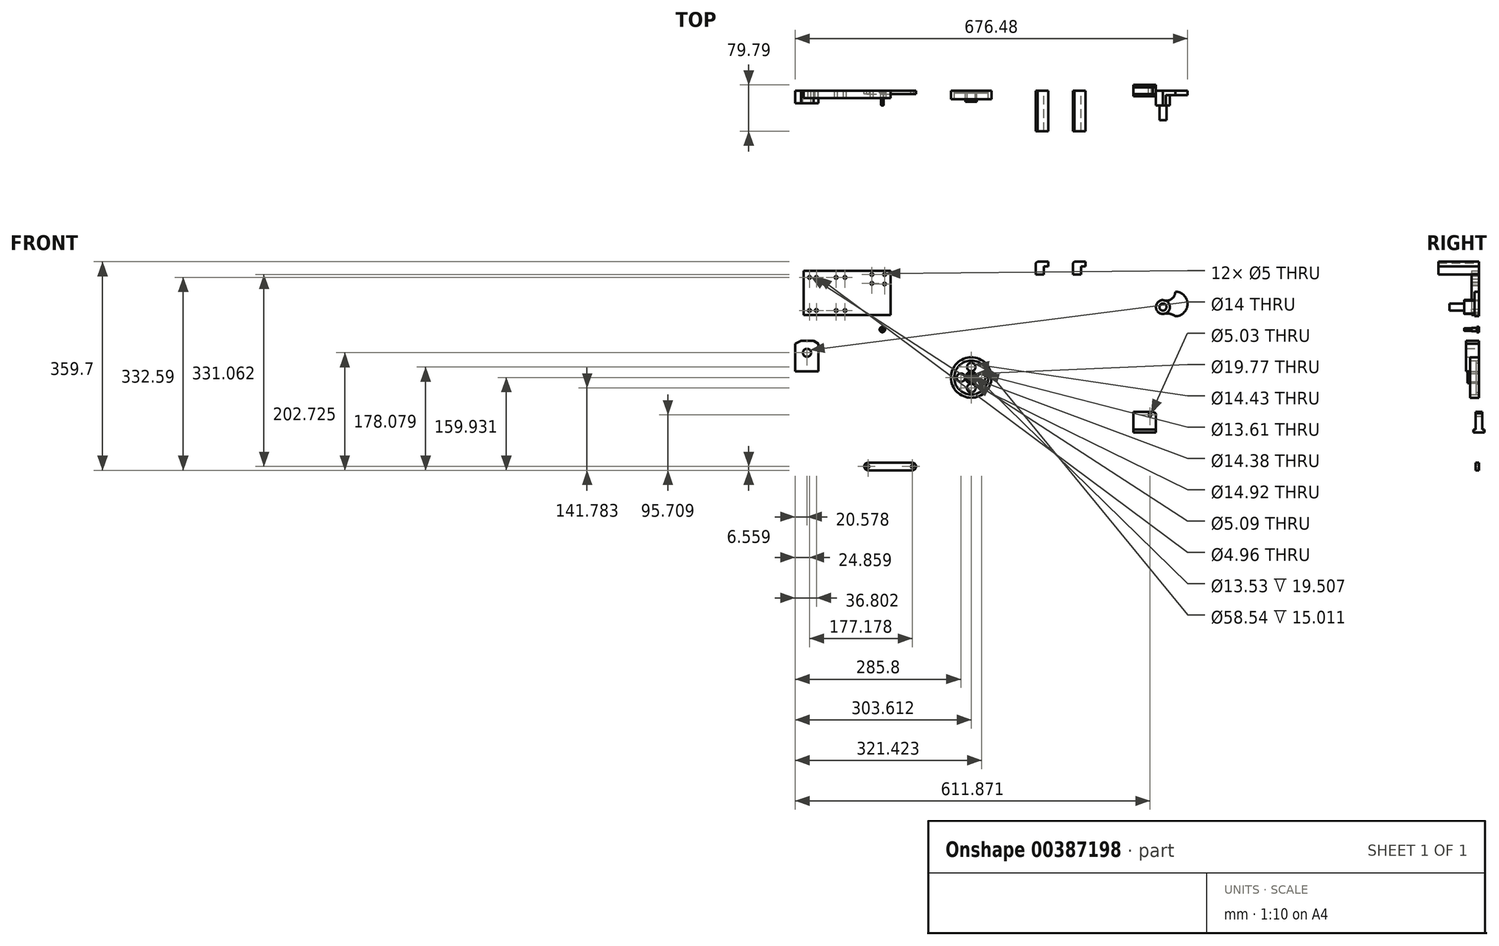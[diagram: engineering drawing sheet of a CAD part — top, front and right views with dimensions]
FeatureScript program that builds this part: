
annotation { "Feature Type Name" : "Feature", "Feature Type Description" : "" }
export const myFeature = defineFeature(function(context is Context, id is Id, definition is map)
    precondition{}
    {
        {
            var Q0;
            Q0=qCreatedBy(makeId("Front.planeOp"),FACE);
            var sketch = newSketch(context, id + "F0", { "sketchPlane" : qUnion([Q0])});
            skLineSegment(sketch, "E0.bottom", {"start": v(-272.23, -114.03) * mm, "end": v(-232.23, -114.03) * mm});
            skLineSegment(sketch, "E0.top", {"start": v(-272.23, -162.01) * mm, "end": v(-232.23, -162.01) * mm});
            skLineSegment(sketch, "E0.left", {"start": v(-272.23, -114.03) * mm, "end": v(-272.23, -162.01) * mm});
            skLineSegment(sketch, "E0.right", {"start": v(-232.23, -114.03) * mm, "end": v(-232.23, -162.01) * mm});
            skLineSegment(sketch, "E1", {"start": v(-232.23, -114.03) * mm, "end": v(-240.58, -109.22) * mm});
            skLineSegment(sketch, "E2", {"start": v(-240.58, -109.22) * mm, "end": v(-262.01, -109.22) * mm});
            skLineSegment(sketch, "E3", {"start": v(-262.01, -109.22) * mm, "end": v(-272.23, -114.03) * mm});
            skCircle(sketch, "E4", {"center": v(-251.65, -129.87) * mm, "radius": 7 * mm});
            skLineSegment(sketch, "E5.bottom", {"start": v(-146.57, -319.47) * mm, "end": v(-70.2, -319.47) * mm});
            skLineSegment(sketch, "E5.top", {"start": v(-146.57, -332.59) * mm, "end": v(-70.2, -332.59) * mm});
            skArc(sketch, "E6", {"start": v(-70.2, -332.59) * mm, "mid": v(-63.64, -326.03) * mm, "end": v(-70.2, -319.47) * mm});
            skArc(sketch, "E7", {"start": v(-146.57, -319.47) * mm, "mid": v(-153.13, -326.03) * mm, "end": v(-146.57, -332.59) * mm});
            skCircle(sketch, "E8", {"center": v(-146.57, -326.03) * mm, "radius": 2.5 * mm});
            skCircle(sketch, "E9", {"center": v(-70.2, -326.03) * mm, "radius": 2.5 * mm});
            skLineSegment(sketch, "E10.bottom", {"start": v(310.57, -262.58) * mm, "end": v(349.62, -262.58) * mm});
            skLineSegment(sketch, "E10.top", {"start": v(310.57, -267.24) * mm, "end": v(349.62, -267.24) * mm});
            skLineSegment(sketch, "E10.left", {"start": v(310.57, -262.58) * mm, "end": v(310.57, -267.24) * mm});
            skLineSegment(sketch, "E10.right", {"start": v(349.62, -262.58) * mm, "end": v(349.62, -267.24) * mm});
            skLineSegment(sketch, "E11.top", {"start": v(310.57, -232.03) * mm, "end": v(344.59, -232.03) * mm});
            skLineSegment(sketch, "E11.left", {"start": v(310.57, -262.58) * mm, "end": v(310.57, -232.03) * mm});
            skLineSegment(sketch, "E11.right", {"start": v(349.62, -262.58) * mm, "end": v(349.62, -234.65) * mm});
            skLineSegment(sketch, "E12", {"start": v(344.59, -232.03) * mm, "end": v(349.62, -234.65) * mm});
            skPoint(sketch, "E13.orphan", {"position": v(349.62, -232.03) * mm});
            skCircle(sketch, "E14", {"center": v(339.64, -236.88) * mm, "radius": 2.52 * mm});
            skLineSegment(sketch, "E15.bottom", {"start": v(-257.4, 11.32) * mm, "end": v(-107.39, 11.32) * mm});
            skLineSegment(sketch, "E15.top", {"start": v(-257.4, -64.67) * mm, "end": v(-107.39, -64.67) * mm});
            skLineSegment(sketch, "E15.left", {"start": v(-257.4, 11.32) * mm, "end": v(-257.4, -64.67) * mm});
            skLineSegment(sketch, "E15.right", {"start": v(-107.39, 11.32) * mm, "end": v(-107.39, -64.67) * mm});
            skCircle(sketch, "E16", {"center": v(-247.37, 0) * mm, "radius": 2.55 * mm});
            skCircle(sketch, "E17", {"center": v(-235.43, 0) * mm, "radius": 2.48 * mm});
            skCircle(sketch, "E18", {"center": v(-235.43, -56.99) * mm, "radius": 2.5 * mm});
            skCircle(sketch, "E19", {"center": v(-247.37, -56.99) * mm, "radius": 2.5 * mm});
            skCircle(sketch, "E20", {"center": v(-201.5, -56.99) * mm, "radius": 2.5 * mm});
            skCircle(sketch, "E21", {"center": v(-186.19, -56.99) * mm, "radius": 2.5 * mm});
            skCircle(sketch, "E22", {"center": v(-201.5, 0) * mm, "radius": 2.5 * mm});
            skCircle(sketch, "E23", {"center": v(-186.19, 0) * mm, "radius": 2.5 * mm});
            skCircle(sketch, "E24", {"center": v(-139.86, 5.03) * mm, "radius": 2.5 * mm});
            skCircle(sketch, "E25", {"center": v(-139.86, -10.28) * mm, "radius": 2.5 * mm});
            skCircle(sketch, "E26", {"center": v(-118.04, 5.03) * mm, "radius": 2.5 * mm});
            skCircle(sketch, "E27", {"center": v(-118.04, -11.43) * mm, "radius": 2.5 * mm});
            skLineSegment(sketch, "E28.bottom", {"start": v(142.44, 5.11) * mm, "end": v(156.44, 5.11) * mm});
            skLineSegment(sketch, "E28.top", {"start": v(142.44, 19.1) * mm, "end": v(156.44, 19.1) * mm});
            skLineSegment(sketch, "E28.left", {"start": v(142.44, 5.11) * mm, "end": v(142.44, 19.1) * mm});
            skLineSegment(sketch, "E28.right", {"start": v(156.44, 5.11) * mm, "end": v(156.44, 19.1) * mm});
            skLineSegment(sketch, "E29.bottom", {"start": v(142.44, 19.1) * mm, "end": v(164.44, 19.1) * mm});
            skLineSegment(sketch, "E29.top", {"start": v(145.53, 27.11) * mm, "end": v(164.44, 27.11) * mm});
            skLineSegment(sketch, "E29.left", {"start": v(142.44, 19.1) * mm, "end": v(142.44, 24.73) * mm});
            skLineSegment(sketch, "E29.right", {"start": v(164.44, 19.1) * mm, "end": v(164.44, 27.11) * mm});
            skLineSegment(sketch, "E30", {"start": v(145.53, 27.11) * mm, "end": v(142.44, 24.73) * mm});
            skPoint(sketch, "E31.oppositeSnap0", {"position": v(153.44, 19.1) * mm});
            skLineSegment(sketch, "E31.bottom", {"start": v(206.6, 5.11) * mm, "end": v(220.6, 5.11) * mm});
            skLineSegment(sketch, "E31.top", {"start": v(206.6, 19.1) * mm, "end": v(220.6, 19.1) * mm});
            skLineSegment(sketch, "E31.left", {"start": v(206.6, 5.11) * mm, "end": v(206.6, 19.1) * mm});
            skLineSegment(sketch, "E31.right", {"start": v(220.6, 5.11) * mm, "end": v(220.6, 19.1) * mm});
            skLineSegment(sketch, "E32.bottom", {"start": v(206.6, 19.1) * mm, "end": v(228.6, 19.1) * mm});
            skLineSegment(sketch, "E32.top", {"start": v(209.4, 27.11) * mm, "end": v(228.6, 27.11) * mm});
            skLineSegment(sketch, "E32.right", {"start": v(228.6, 19.1) * mm, "end": v(228.6, 27.11) * mm});
            skLineSegment(sketch, "E33", {"start": v(209.4, 27.11) * mm, "end": v(206.6, 24.7) * mm});
            skLineSegment(sketch, "E34", {"start": v(206.6, 24.7) * mm, "end": v(206.6, 19.1) * mm});
            skCircle(sketch, "E35", {"center": v(-121.83, -89.85) * mm, "radius": 2 * mm});
            skCircle(sketch, "E36", {"center": v(-121.83, -89.85) * mm, "radius": 2.87 * mm});
            skCircle(sketch, "E37", {"center": v(-121.83, -89.85) * mm, "radius": 4.6 * mm});
            skArc(sketch, "E38", {"start": v(383.1, -66.86) * mm, "mid": v(404.25, -45.72) * mm, "end": v(383.1, -24.58) * mm});
            skLineSegment(sketch, "E39", {"start": v(383.1, -24.58) * mm, "end": v(383.1, -66.86) * mm});
            skArc(sketch, "E40", {"start": v(361.79, -39) * mm, "mid": v(376.27, -37.44) * mm, "end": v(383.1, -24.58) * mm});
            skCircle(sketch, "E41", {"center": v(361.79, -51.03) * mm, "radius": 12.04 * mm});
            skArc(sketch, "E42", {"start": v(383.1, -66.86) * mm, "mid": v(372.87, -62.57) * mm, "end": v(361.79, -63.07) * mm});
            skCircle(sketch, "E43", {"center": v(361.79, -51.03) * mm, "radius": 6.14 * mm});
            skCircle(sketch, "E44", {"center": v(31.38, -172.66) * mm, "radius": 34.87 * mm});
            skCircle(sketch, "E45", {"center": v(31.38, -172.66) * mm, "radius": 29.27 * mm});
            skCircle(sketch, "E46", {"center": v(31.38, -172.66) * mm, "radius": 9.88 * mm});
            skCircle(sketch, "E47", {"center": v(31.38, -172.66) * mm, "radius": 6.76 * mm});
            skCircle(sketch, "E48", {"center": v(31.38, -154.51) * mm, "radius": 7.22 * mm});
            skCircle(sketch, "E49", {"center": v(49.2, -172.66) * mm, "radius": 6.8 * mm});
            skCircle(sketch, "E50", {"center": v(13.57, -172.66) * mm, "radius": 7.2 * mm});
            skCircle(sketch, "E51", {"center": v(31.38, -190.8) * mm, "radius": 7.46 * mm});
            skSolve(sketch);
        }
        {
            var Q0;
            Q0=makeQuery(id+"F0.imprint","IMPRINT",FACE,{"disambiguationData":[TD([[makeQuery(id+"F0.imprint","IMPRINT",EDGE,{"derivedFrom":sQuery(id+"F0.wireOp",EDGE,"E35")}),1.0]])]});
            extrude(context, id + "F1", {"entities" : qUnion([Q0]), "depth" : 25.4 * mm});
        }
        {
            var Q0;
            Q0=makeQuery(id+"F0.imprint","IMPRINT",FACE,{"disambiguationData":[TD([[makeQuery(id+"F0.imprint","IMPRINT",EDGE,{"derivedFrom":sQuery(id+"F0.wireOp",EDGE,"E35")}),-1.0]])]});
            extrude(context, id + "F2", {"entities" : qUnion([Q0]), "operationType" : NewBodyOperationType.ADD, "depth" : 12.7 * mm});
        }
        {
            var Q0;
            Q0=makeQuery(id+"F0.imprint","IMPRINT",FACE,{"disambiguationData":[TD([[makeQuery(id+"F0.imprint","IMPRINT",EDGE,{"derivedFrom":sQuery(id+"F0.wireOp",EDGE,"E36")}),-1.0]])]});
            extrude(context, id + "F3", {"entities" : qUnion([Q0]), "operationType" : NewBodyOperationType.ADD, "depth" : 3.8 * mm});
        }
        {
            var Q0;
            Q0=makeQuery(id+"F3.opExtrude","CAP_EDGE",EDGE,{"disambiguationData":[OSD([sQuery(id+"F0.wireOp",EDGE,"E37")])],"isStart":true});
            var Q1;
            Q1=makeQuery(id+"F1.opExtrude","CAP_EDGE",EDGE,{"disambiguationData":[OSD([sQuery(id+"F0.wireOp",EDGE,"E35")])],"isStart":false});
            fillet(context, id + "F4", {"entities" : qUnion([Q0, Q1]), "radius" : 0.5 * mm, "tangentPropagation" : true, "allowEdgeOverflow" : false});
        }
        {
            var Q0;
            Q0=makeQuery(id+"F0.imprint","IMPRINT",FACE,{"disambiguationData":[TD([[makeQuery(id+"F0.imprint","IMPRINT",EDGE,{"derivedFrom":sQuery(id+"F0.wireOp",EDGE,"E43")}),1.0]])]});
            extrude(context, id + "F5", {"entities" : qUnion([Q0]), "depth" : 50.8 * mm});
        }
        {
            var Q0;
            Q0=makeQuery(id+"F0.imprint","IMPRINT",FACE,{"disambiguationData":[TD([[makeQuery(id+"F0.imprint","IMPRINT",EDGE,{"derivedFrom":sQuery(id+"F0.wireOp",EDGE,"E43")}),-1.0]])]});
            extrude(context, id + "F6", {"entities" : qUnion([Q0]), "operationType" : NewBodyOperationType.ADD, "depth" : 25.4 * mm});
        }
        {
            var Q0;
            Q0=makeQuery(id+"F0.imprint","IMPRINT",FACE,{"disambiguationData":[TD([[makeQuery(id+"F0.imprint","IMPRINT",EDGE,{"derivedFrom":sQuery(id+"F0.wireOp",EDGE,"E38")}),1.0]])]});
            var Q1;
            {var subQ0=sQuery(id+"F0.wireOp",EDGE,"E39");Q1=makeQuery(id+"F0.imprint","IMPRINT",FACE,{"disambiguationData":[TD([[makeQuery(id+"F0.imprint","IMPRINT",EDGE,{"derivedFrom":subQ0}),-1.0]])]});}
            extrude(context, id + "F7", {"entities" : qUnion([Q0, Q1]), "operationType" : NewBodyOperationType.ADD, "depth" : 7.62 * mm});
        }
        {
            var Q0;
            Q0=makeQuery(id+"F0.imprint","IMPRINT",FACE,{"disambiguationData":[TD([[makeQuery(id+"F0.imprint","IMPRINT",EDGE,{"derivedFrom":sQuery(id+"F0.wireOp",EDGE,"E46")}),1.0]])]});
            extrude(context, id + "F8", {"entities" : qUnion([Q0]), "depth" : 19.5 * mm});
        }
        {
            var Q0;
            Q0=makeQuery(id+"F0.imprint","IMPRINT",FACE,{"disambiguationData":[TD([[makeQuery(id+"F0.imprint","IMPRINT",EDGE,{"derivedFrom":sQuery(id+"F0.wireOp",EDGE,"E44")}),1.0]])]});
            extrude(context, id + "F9", {"entities" : qUnion([Q0]), "depth" : 15 * mm});
        }
        {
            var Q0;
            Q0=makeQuery(id+"F0.imprint","IMPRINT",FACE,{"disambiguationData":[TD([[makeQuery(id+"F0.imprint","IMPRINT",EDGE,{"derivedFrom":sQuery(id+"F0.wireOp",EDGE,"E45")}),1.0]])]});
            extrude(context, id + "F10", {"entities" : qUnion([Q0]), "depth" : 4.24 * mm});
        }
        {
            var Q0;
            Q0=makeQuery(id+"F0.imprint","IMPRINT",FACE,{"disambiguationData":[TD([[makeQuery(id+"F0.imprint","IMPRINT",EDGE,{"derivedFrom":sQuery(id+"F0.wireOp",EDGE,"E15.bottom")}),-1.0]])]});
            extrude(context, id + "F11", {"entities" : qUnion([Q0]), "depth" : 12.7 * mm});
        }
        {
            var Q0;
            Q0=makeQuery(id+"F0.imprint","IMPRINT",FACE,{"disambiguationData":[TD([[makeQuery(id+"F0.imprint","IMPRINT",EDGE,{"derivedFrom":sQuery(id+"F0.wireOp",EDGE,"E0.bottom")}),-1.0]])]});
            var Q1;
            Q1=makeQuery(id+"F0.imprint","IMPRINT",FACE,{"disambiguationData":[TD([[makeQuery(id+"F0.imprint","IMPRINT",EDGE,{"derivedFrom":sQuery(id+"F0.wireOp",EDGE,"E0.bottom")}),1.0]])]});
            extrude(context, id + "F12", {"entities" : qUnion([Q0, Q1]), "depth" : 22 * mm});
        }
        {
            var Q0;
            Q0=makeQuery(id+"F0.imprint","IMPRINT",FACE,{"disambiguationData":[TD([[makeQuery(id+"F0.imprint","IMPRINT",EDGE,{"derivedFrom":sQuery(id+"F0.wireOp",EDGE,"E10.top")}),1.0]])]});
            extrude(context, id + "F13", {"entities" : qUnion([Q0]), "endBound" : BoundingType.SYMMETRIC, "depth" : 19.58 * mm});
        }
        {
            var Q0;
            Q0=makeQuery(id+"F0.imprint","IMPRINT",FACE,{"disambiguationData":[TD([[makeQuery(id+"F0.imprint","IMPRINT",EDGE,{"derivedFrom":sQuery(id+"F0.wireOp",EDGE,"E11.top")}),-1.0]])]});
            extrude(context, id + "F14", {"entities" : qUnion([Q0]), "operationType" : NewBodyOperationType.ADD, "endBound" : BoundingType.SYMMETRIC, "depth" : 11.58 * mm});
        }
        {
            var Q0;
            Q0=makeQuery(id+"F0.imprint","IMPRINT",FACE,{"disambiguationData":[TD([[makeQuery(id+"F0.imprint","IMPRINT",EDGE,{"derivedFrom":sQuery(id+"F0.wireOp",EDGE,"E5.bottom")}),-1.0]])]});
            extrude(context, id + "F15", {"entities" : qUnion([Q0]), "depth" : 5.66 * mm});
        }
        {
            var Q0;
            Q0=makeQuery(id+"F0.imprint","IMPRINT",FACE,{"disambiguationData":[TD([[makeQuery(id+"F0.imprint","IMPRINT",EDGE,{"derivedFrom":sQuery(id+"F0.wireOp",EDGE,"E31.bottom")}),1.0]])]});
            var Q1;
            Q1=makeQuery(id+"F0.imprint","IMPRINT",FACE,{"disambiguationData":[TD([[makeQuery(id+"F0.imprint","IMPRINT",EDGE,{"derivedFrom":sQuery(id+"F0.wireOp",EDGE,"E32.top")}),-1.0]])]});
            var Q2;
            Q2=makeQuery(id+"F0.imprint","IMPRINT",FACE,{"disambiguationData":[TD([[makeQuery(id+"F0.imprint","IMPRINT",EDGE,{"derivedFrom":sQuery(id+"F0.wireOp",EDGE,"E28.bottom")}),1.0]])]});
            var Q3;
            Q3=makeQuery(id+"F0.imprint","IMPRINT",FACE,{"disambiguationData":[TD([[makeQuery(id+"F0.imprint","IMPRINT",EDGE,{"derivedFrom":sQuery(id+"F0.wireOp",EDGE,"E29.top")}),-1.0]])]});
            extrude(context, id + "F16", {"entities" : qUnion([Q0, Q1, Q2, Q3]), "depth" : 70 * mm});
        }
    });
